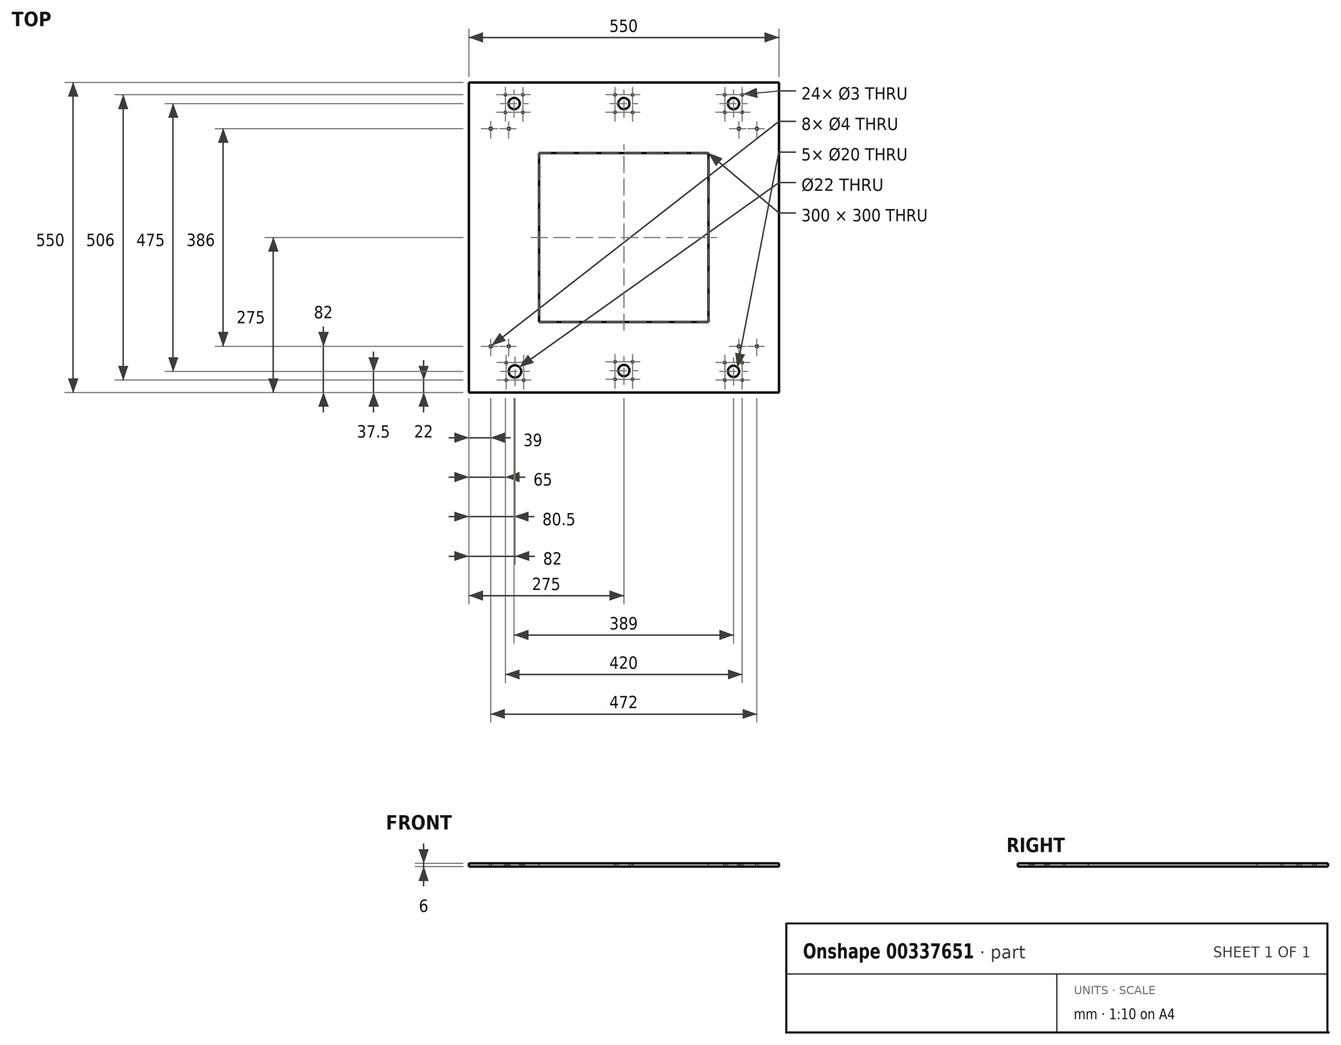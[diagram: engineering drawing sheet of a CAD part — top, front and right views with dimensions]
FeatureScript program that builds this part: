
annotation { "Feature Type Name" : "Feature", "Feature Type Description" : "" }
export const myFeature = defineFeature(function(context is Context, id is Id, definition is map)
    precondition{}
    {
        {
            var Q0;
            Q0=qCreatedBy(makeId("Top.planeOp"),FACE);
            var sketch = newSketch(context, id + "F0", { "sketchPlane" : qUnion([Q0])});
            skLineSegment(sketch, "E0.bottom", {"start": v(275, -275) * mm, "end": v(-275, -275) * mm});
            skLineSegment(sketch, "E0.top", {"start": v(275, 275) * mm, "end": v(-275, 275) * mm});
            skLineSegment(sketch, "E0.left", {"start": v(275, -275) * mm, "end": v(275, 275) * mm});
            skLineSegment(sketch, "E0.right", {"start": v(-275, -275) * mm, "end": v(-275, 275) * mm});
            skPoint(sketch, "E0.middle", {"position": v(0, 0) * mm});
            skSolve(sketch);
        }
        {
            var Q0;
            Q0 = qSketchRegion(id + "F0", true);
            extrude(context, id + "F1", {"entities" : qUnion([Q0]), "depth" : 6 * mm});
        }
        {
            var Q0;
            Q0=makeQuery(id+"F1.opExtrude","CAP_FACE",FACE,{"disambiguationData":[OSD([sQuery(id+"F0.wireOp",EDGE,"E0.bottom"),sQuery(id+"F0.wireOp",EDGE,"E0.top"),sQuery(id+"F0.wireOp",EDGE,"E0.left"),sQuery(id+"F0.wireOp",EDGE,"E0.right")])],"isStart":false});
            var sketch = newSketch(context, id + "F2", { "sketchPlane" : qUnion([Q0])});
            skLineSegment(sketch, "E1.bottom", {"start": v(150, -150) * mm, "end": v(-150, -150) * mm});
            skLineSegment(sketch, "E1.top", {"start": v(150, 150) * mm, "end": v(-150, 150) * mm});
            skLineSegment(sketch, "E1.left", {"start": v(150, -150) * mm, "end": v(150, 150) * mm});
            skLineSegment(sketch, "E1.right", {"start": v(-150, -150) * mm, "end": v(-150, 150) * mm});
            skPoint(sketch, "E1.middle", {"position": v(0, 0) * mm});
            skSolve(sketch);
        }
        {
            var Q0;
            Q0 = qSketchRegion(id + "F2", true);
            extrude(context, id + "F3", {"entities" : qUnion([Q0]), "operationType" : NewBodyOperationType.REMOVE, "endBound" : BoundingType.UP_TO_NEXT, "oppositeDirection" : true, "depth" : 10 * mm});
        }
        {
            var Q0;
            Q0=makeQuery(id+"F1.opExtrude","CAP_FACE",FACE,{"disambiguationData":[OSD([sQuery(id+"F0.wireOp",EDGE,"E0.bottom"),sQuery(id+"F0.wireOp",EDGE,"E0.top"),sQuery(id+"F0.wireOp",EDGE,"E0.left"),sQuery(id+"F0.wireOp",EDGE,"E0.right")])],"isStart":false});
            var sketch = newSketch(context, id + "F4", { "sketchPlane" : qUnion([Q0])});
            skPoint(sketch, "E2", {"position": v(-194.5, 237.5) * mm});
            skLineSegment(sketch, "E3.bottom", {"start": v(-179, 222) * mm, "end": v(-210, 222) * mm, "construction": true});
            skLineSegment(sketch, "E3.top", {"start": v(-179, 253) * mm, "end": v(-210, 253) * mm, "construction": true});
            skLineSegment(sketch, "E3.left", {"start": v(-179, 222) * mm, "end": v(-179, 253) * mm, "construction": true});
            skLineSegment(sketch, "E3.right", {"start": v(-210, 222) * mm, "end": v(-210, 253) * mm, "construction": true});
            skCircle(sketch, "E4", {"center": v(-179, 253) * mm, "radius": 1.5 * mm});
            skCircle(sketch, "E5", {"center": v(-210, 253) * mm, "radius": 1.5 * mm});
            skCircle(sketch, "E6", {"center": v(-210, 222) * mm, "radius": 1.5 * mm});
            skCircle(sketch, "E7", {"center": v(-179, 222) * mm, "radius": 1.5 * mm});
            skCircle(sketch, "E8", {"center": v(-194.5, 237.5) * mm, "radius": 10 * mm});
            skPoint(sketch, "E9", {"position": v(194.5, 237.5) * mm});
            skLineSegment(sketch, "E10.bottom", {"start": v(210, 222) * mm, "end": v(179, 222) * mm, "construction": true});
            skLineSegment(sketch, "E10.top", {"start": v(210, 253) * mm, "end": v(179, 253) * mm, "construction": true});
            skLineSegment(sketch, "E10.left", {"start": v(210, 222) * mm, "end": v(210, 253) * mm, "construction": true});
            skLineSegment(sketch, "E10.right", {"start": v(179, 222) * mm, "end": v(179, 253) * mm, "construction": true});
            skCircle(sketch, "E11", {"center": v(210, 253) * mm, "radius": 1.5 * mm});
            skCircle(sketch, "E12", {"center": v(179, 253) * mm, "radius": 1.5 * mm});
            skCircle(sketch, "E13", {"center": v(179, 222) * mm, "radius": 1.5 * mm});
            skCircle(sketch, "E14", {"center": v(210, 222) * mm, "radius": 1.5 * mm});
            skCircle(sketch, "E15", {"center": v(194.5, 237.5) * mm, "radius": 10 * mm});
            skPoint(sketch, "E16", {"position": v(0, 237.5) * mm});
            skLineSegment(sketch, "E17.bottom", {"start": v(15.5, 222) * mm, "end": v(-15.5, 222) * mm, "construction": true});
            skLineSegment(sketch, "E17.top", {"start": v(15.5, 253) * mm, "end": v(-15.5, 253) * mm, "construction": true});
            skLineSegment(sketch, "E17.left", {"start": v(15.5, 222) * mm, "end": v(15.5, 253) * mm, "construction": true});
            skLineSegment(sketch, "E17.right", {"start": v(-15.5, 222) * mm, "end": v(-15.5, 253) * mm, "construction": true});
            skCircle(sketch, "E18", {"center": v(15.5, 253) * mm, "radius": 1.5 * mm});
            skCircle(sketch, "E19", {"center": v(-15.5, 253) * mm, "radius": 1.5 * mm});
            skCircle(sketch, "E20", {"center": v(-15.5, 222) * mm, "radius": 1.5 * mm});
            skCircle(sketch, "E21", {"center": v(15.5, 222) * mm, "radius": 1.5 * mm});
            skCircle(sketch, "E22", {"center": v(0, 237.5) * mm, "radius": 10 * mm});
            skPoint(sketch, "E23", {"position": v(-193, -237.5) * mm});
            skLineSegment(sketch, "E24.bottom", {"start": v(-177.5, -253) * mm, "end": v(-208.5, -253) * mm, "construction": true});
            skLineSegment(sketch, "E24.top", {"start": v(-177.5, -222) * mm, "end": v(-208.5, -222) * mm, "construction": true});
            skLineSegment(sketch, "E24.left", {"start": v(-177.5, -253) * mm, "end": v(-177.5, -222) * mm, "construction": true});
            skLineSegment(sketch, "E24.right", {"start": v(-208.5, -253) * mm, "end": v(-208.5, -222) * mm, "construction": true});
            skCircle(sketch, "E25", {"center": v(-177.5, -222) * mm, "radius": 1.5 * mm});
            skCircle(sketch, "E26", {"center": v(-208.5, -222) * mm, "radius": 1.5 * mm});
            skCircle(sketch, "E27", {"center": v(-208.5, -253) * mm, "radius": 1.5 * mm});
            skCircle(sketch, "E28", {"center": v(-177.5, -253) * mm, "radius": 1.5 * mm});
            skCircle(sketch, "E29", {"center": v(-193, -237.5) * mm, "radius": 11 * mm});
            skPoint(sketch, "E30", {"position": v(194.5, -237.5) * mm});
            skLineSegment(sketch, "E31.bottom", {"start": v(210, -253) * mm, "end": v(179, -253) * mm, "construction": true});
            skLineSegment(sketch, "E31.top", {"start": v(210, -222) * mm, "end": v(179, -222) * mm, "construction": true});
            skLineSegment(sketch, "E31.left", {"start": v(210, -253) * mm, "end": v(210, -222) * mm, "construction": true});
            skLineSegment(sketch, "E31.right", {"start": v(179, -253) * mm, "end": v(179, -222) * mm, "construction": true});
            skCircle(sketch, "E32", {"center": v(210, -222) * mm, "radius": 1.5 * mm});
            skCircle(sketch, "E33", {"center": v(179, -222) * mm, "radius": 1.5 * mm});
            skCircle(sketch, "E34", {"center": v(179, -253) * mm, "radius": 1.5 * mm});
            skCircle(sketch, "E35", {"center": v(210, -253) * mm, "radius": 1.5 * mm});
            skCircle(sketch, "E36", {"center": v(194.5, -237.5) * mm, "radius": 10 * mm});
            skPoint(sketch, "E37", {"position": v(0, -236) * mm});
            skLineSegment(sketch, "E38.bottom", {"start": v(15.5, -251.5) * mm, "end": v(-15.5, -251.5) * mm, "construction": true});
            skLineSegment(sketch, "E38.top", {"start": v(15.5, -220.5) * mm, "end": v(-15.5, -220.5) * mm, "construction": true});
            skLineSegment(sketch, "E38.left", {"start": v(15.5, -251.5) * mm, "end": v(15.5, -220.5) * mm, "construction": true});
            skLineSegment(sketch, "E38.right", {"start": v(-15.5, -251.5) * mm, "end": v(-15.5, -220.5) * mm, "construction": true});
            skCircle(sketch, "E39", {"center": v(15.5, -220.5) * mm, "radius": 1.5 * mm});
            skCircle(sketch, "E40", {"center": v(-15.5, -220.5) * mm, "radius": 1.5 * mm});
            skCircle(sketch, "E41", {"center": v(-15.5, -251.5) * mm, "radius": 1.5 * mm});
            skCircle(sketch, "E42", {"center": v(15.5, -251.5) * mm, "radius": 1.5 * mm});
            skCircle(sketch, "E43", {"center": v(0, -236) * mm, "radius": 10 * mm});
            skPoint(sketch, "E44", {"position": v(0, -150) * mm});
            skPoint(sketch, "E45", {"position": v(0, -275) * mm});
            skLineSegment(sketch, "E46", {"start": v(0, -150) * mm, "end": v(0, -275) * mm, "construction": true});
            skPoint(sketch, "E47", {"position": v(150, 0) * mm});
            skPoint(sketch, "E48", {"position": v(275, 0) * mm});
            skLineSegment(sketch, "E49", {"start": v(150, 0) * mm, "end": v(275, 0) * mm, "construction": true});
            skLineSegment(sketch, "E50", {"start": v(-236, 193) * mm, "end": v(-204, 193) * mm, "construction": true});
            skCircle(sketch, "E51", {"center": v(-236, 193) * mm, "radius": 2 * mm});
            skCircle(sketch, "E52", {"center": v(-204, 193) * mm, "radius": 2 * mm});
            skPoint(sketch, "E53", {"position": v(-236, -193) * mm});
            skPoint(sketch, "E54", {"position": v(-204, -193) * mm});
            skCircle(sketch, "E55", {"center": v(-236, -193) * mm, "radius": 2 * mm});
            skCircle(sketch, "E56", {"center": v(-204, -193) * mm, "radius": 2 * mm});
            skPoint(sketch, "E57", {"position": v(204, -193) * mm});
            skPoint(sketch, "E58", {"position": v(236, -193) * mm});
            skCircle(sketch, "E59", {"center": v(236, -193) * mm, "radius": 2 * mm});
            skCircle(sketch, "E60", {"center": v(204, -193) * mm, "radius": 2 * mm});
            skPoint(sketch, "E61", {"position": v(204, 193) * mm});
            skPoint(sketch, "E62", {"position": v(236, 193) * mm});
            skCircle(sketch, "E63", {"center": v(204, 193) * mm, "radius": 2 * mm});
            skCircle(sketch, "E64", {"center": v(236, 193) * mm, "radius": 2 * mm});
            skLineSegment(sketch, "E65", {"start": v(-204, -193) * mm, "end": v(-236, -193) * mm, "construction": true});
            skPoint(sketch, "E66.endSnap0", {"position": v(-150, 0) * mm});
            skLineSegment(sketch, "E67", {"start": v(-150, 0) * mm, "end": v(-275, 0) * mm, "construction": true});
            skLineSegment(sketch, "E68", {"start": v(236, 193) * mm, "end": v(204, 193) * mm, "construction": true});
            skLineSegment(sketch, "E69", {"start": v(236, -193) * mm, "end": v(236, -193) * mm});
            skLineSegment(sketch, "E70", {"start": v(204, -193) * mm, "end": v(236, -193) * mm, "construction": true});
            skLineSegment(sketch, "E71", {"start": v(0, 150) * mm, "end": v(0, 275) * mm, "construction": true});
            skSolve(sketch);
        }
        {
            var Q0;
            Q0 = qSketchRegion(id + "F4", true);
            var Q1;
            Q1=makeQuery(id+"F0.imprint","IMPRINT",FACE,{"disambiguationData":[TD([[makeQuery(id+"F0.imprint","IMPRINT",EDGE,{"derivedFrom":sQuery(id+"F0.wireOp",EDGE,"E0.bottom")}),-1.0]])]});
            extrude(context, id + "F5", {"entities" : qUnion([Q0, Q1]), "operationType" : NewBodyOperationType.REMOVE, "oppositeDirection" : true, "depth" : 25 * mm});
        }
    });
